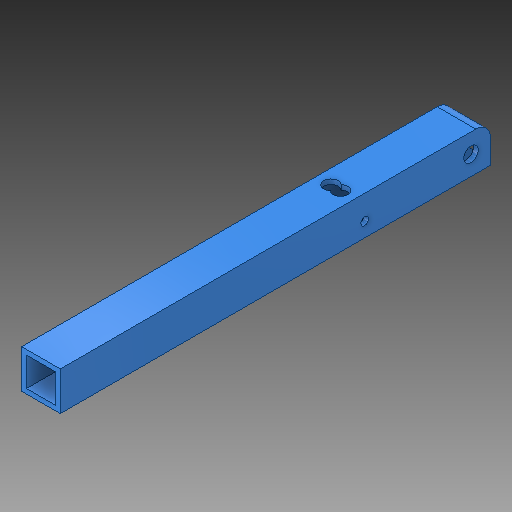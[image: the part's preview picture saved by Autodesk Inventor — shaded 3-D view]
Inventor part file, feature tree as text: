
AUTODESK INVENTOR PART (.ipt)
format: ipt  version: 2017 SP1 (Build 210196100, 196)  size: 139,776 bytes
history: native  units: in
note: dims shown in document units (in); Inventor stores cm internally (conversion verified against a paired STEP export)
features: extrude x3, sketch x3, fillet x1
ambient origin geometry x8: Origin, YZ Plane, XZ Plane, XY Plane, X Axis, Y Axis, Z Axis, Center Point
bodies: Solid1 (feature_tree)
feature tree (7):
  extrude  "Extrusion1"  Depth=0.125in
  extrude  "Extrusion2"  Depth=0.375in
  extrude  "Extrusion3"  Depth=0.125in TaperAngle=0.0deg
  fillet  "Fillet1"  Radius=0.375in
  sketch  "Sketch1"  dims[d0=1.0in d1=0.125in]
  sketch  "Sketch2"  dims[d2=11.125in d3=0.0in d4=0.375in]
  sketch  "Sketch3"  dims[d5=0.5in d6=5.5in d7=0.0in d8=0.375in d10=5.5in d11=0.0in d12=3.5in d13=0.375in d14=0.375in d15=0.125in d16=0.375in d19=0.2in d20=2.75in d21=0.125in]
